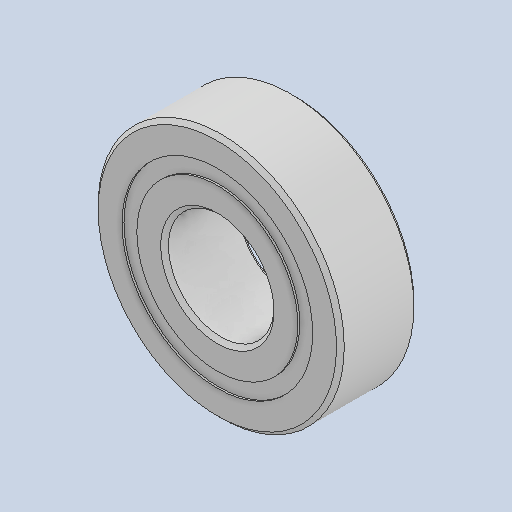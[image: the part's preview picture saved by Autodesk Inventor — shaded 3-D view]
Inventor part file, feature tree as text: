
AUTODESK INVENTOR PART (.ipt)
format: ipt  version: 2022 (Build 260153000, 153)  size: 591,360 bytes
history: native  units: in
note: dims shown in document units (in); Inventor stores cm internally (conversion verified against a paired STEP export)
features: other x11, revolve x5
ambient origin geometry x8: Origin, YZ Plane, XZ Plane, XY Plane, X Axis, Y Axis, Z Axis, Center Point
bodies: Solid1 (feature_tree), Solid2 (feature_tree), Solid3 (feature_tree), Solid4 (feature_tree), Solid5 (feature_tree), Solid6 (feature_tree), Solid7 (feature_tree), Solid8 (feature_tree), Solid9 (feature_tree), Solid10 (feature_tree), Solid11 (feature_tree), Solid12 (feature_tree), Solid13 (feature_tree), Solid14 (feature_tree), Solid15 (feature_tree), Solid16 (feature_tree)
feature tree (16):
  revolve  "Revolve1"  [1 undecoded]
  revolve  "Revolve3"  [1 undecoded]
  revolve  "Revolve4"  [1 undecoded]
  other  "CirPattern1[1]"
  other  "CirPattern1[2]"
  other  "CirPattern1[3]"
  other  "CirPattern1[4]"
  other  "CirPattern1[5]"
  other  "CirPattern1[6]"
  other  "CirPattern1[7]"
  other  "CirPattern1[8]"
  other  "CirPattern1[9]"
  other  "CirPattern1[10]"
  other  "CirPattern1[11]"
  revolve  "Revolve5[1]"  [1 undecoded]
  revolve  "Revolve5[2]"  [1 undecoded]
note: 5 required parameter values undecoded (feature->parameter linkage not recoverable at this tier; creation-order binding heuristic only, values carry confidence <= 0.55)
